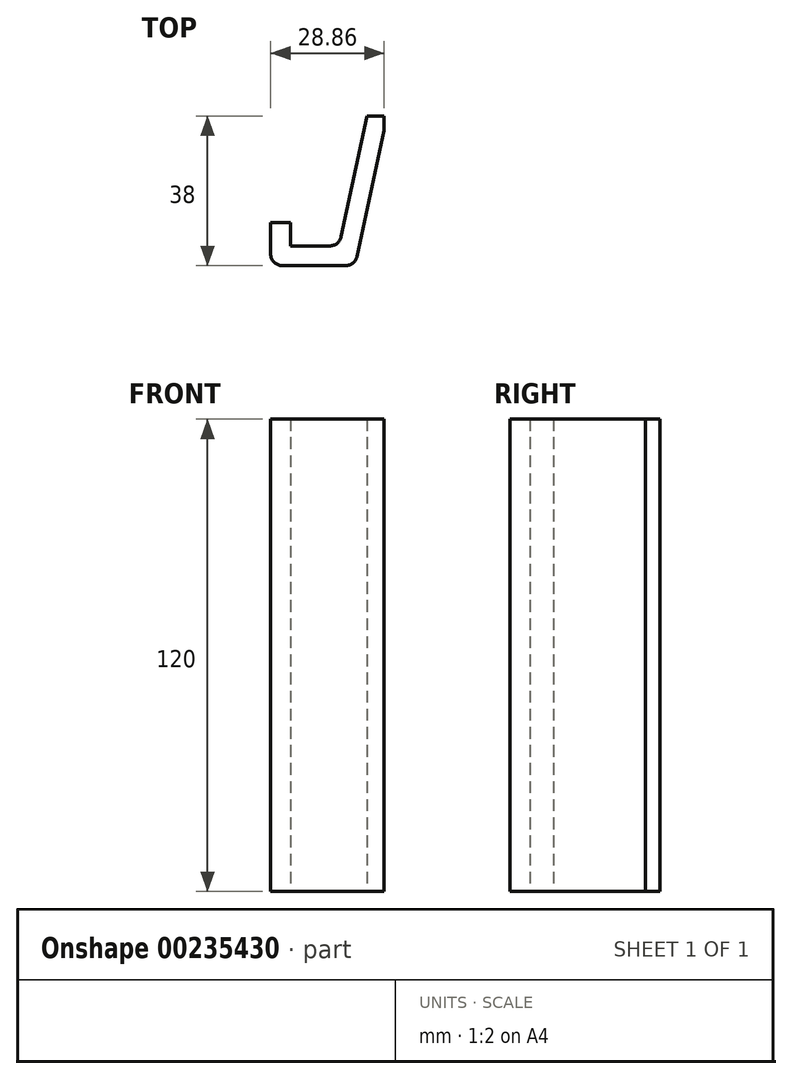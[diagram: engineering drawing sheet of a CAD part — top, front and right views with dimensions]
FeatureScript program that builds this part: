
annotation { "Feature Type Name" : "Feature", "Feature Type Description" : "" }
export const myFeature = defineFeature(function(context is Context, id is Id, definition is map)
    precondition{}
    {
        {
            var Q0;
            Q0=qCreatedBy(makeId("Top.planeOp"),FACE);
            var sketch = newSketch(context, id + "F0", { "sketchPlane" : qUnion([Q0])});
            skLineSegment(sketch, "E0", {"start": v(-25.6, 0) * mm, "end": v(-10.6, 0) * mm});
            skLineSegment(sketch, "E1", {"start": v(-7.67, 2.37) * mm, "end": v(-0.78, 34.37) * mm});
            skLineSegment(sketch, "E2", {"start": v(-5.11, 38) * mm, "end": v(-11.71, 7.37) * mm});
            skLineSegment(sketch, "E3", {"start": v(-14.64, 5) * mm, "end": v(-24.64, 5) * mm});
            skLineSegment(sketch, "E4", {"start": v(-24.64, 5) * mm, "end": v(-24.64, 11) * mm});
            skLineSegment(sketch, "E5", {"start": v(-26.64, 0) * mm, "end": v(-25.6, 0) * mm});
            skPoint(sketch, "E6.visualSharp", {"position": v(-34.64, 0) * mm});
            skArc(sketch, "E6.filletArc", {"start": v(-29.64, 3) * mm, "mid": v(-28.77, 0.88) * mm, "end": v(-26.64, 0) * mm});
            skPoint(sketch, "E7.visualSharp", {"position": v(-8.18, 0) * mm});
            skArc(sketch, "E7.filletArc", {"start": v(-10.6, 0) * mm, "mid": v(-8.72, 0.67) * mm, "end": v(-7.67, 2.37) * mm});
            skPoint(sketch, "E8.visualSharp", {"position": v(-12.22, 5) * mm});
            skArc(sketch, "E8.filletArc", {"start": v(-14.64, 5) * mm, "mid": v(-12.76, 5.67) * mm, "end": v(-11.71, 7.37) * mm});
            skLineSegment(sketch, "E9", {"start": v(-29.64, 3) * mm, "end": v(-29.64, 11) * mm});
            skLineSegment(sketch, "E10", {"start": v(-29.64, 11) * mm, "end": v(-24.64, 11) * mm});
            skLineSegment(sketch, "E11", {"start": v(-5.11, 38) * mm, "end": v(-0.78, 38) * mm});
            skLineSegment(sketch, "E12", {"start": v(-0.78, 38) * mm, "end": v(-0.78, 34.37) * mm});
            skSolve(sketch);
        }
        {
            var Q0;
            Q0=makeQuery(id+"F0.imprint","IMPRINT",FACE,{"disambiguationData":[TD([[makeQuery(id+"F0.imprint","IMPRINT",EDGE,{"derivedFrom":sQuery(id+"F0.wireOp",EDGE,"E0")}),1.0]])]});
            extrude(context, id + "F1", {"entities" : qUnion([Q0]), "depth" : 120 * mm});
        }
    });
